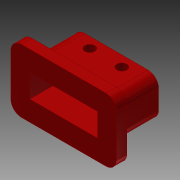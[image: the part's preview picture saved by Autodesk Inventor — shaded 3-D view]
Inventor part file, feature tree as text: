
AUTODESK INVENTOR PART (.ipt)
format: ipt  version: 2015 (Build 190159000, 159)  size: 135,168 bytes
history: native  units: in
note: dims shown in document units (in); Inventor stores cm internally (conversion verified against a paired STEP export)
features: extrude x3, sketch x3, shell x1, fillet x1
ambient origin geometry x8: Origin, YZ Plane, XZ Plane, XY Plane, X Axis, Y Axis, Z Axis, Center Point
bodies: Solid1 (feature_tree)
feature tree (8):
  extrude  "Extrusion1"  Depth=0.474in
  shell  "Shell1"  Thickness=0.5in
  extrude  "Extrusion2"  Depth=0.125in
  extrude  "Extrusion3"  Depth=0.125in
  fillet  "Fillet1"  Radius=0.5in
  sketch  "Sketch1"  dims[d0=1.0in d1=0.474in d2=0.5in d3=0.0in]
  sketch  "Sketch2"  dims[d4=0.1in d23=0.125in]
  sketch  "Sketch3"  dims[d24=0.12in d25=0.38in d26=0.5in d27=0.0in d28=0.75in d29=1.25in d30=0.125in d31=0.125in d32=0.0in d33=0.125in]
